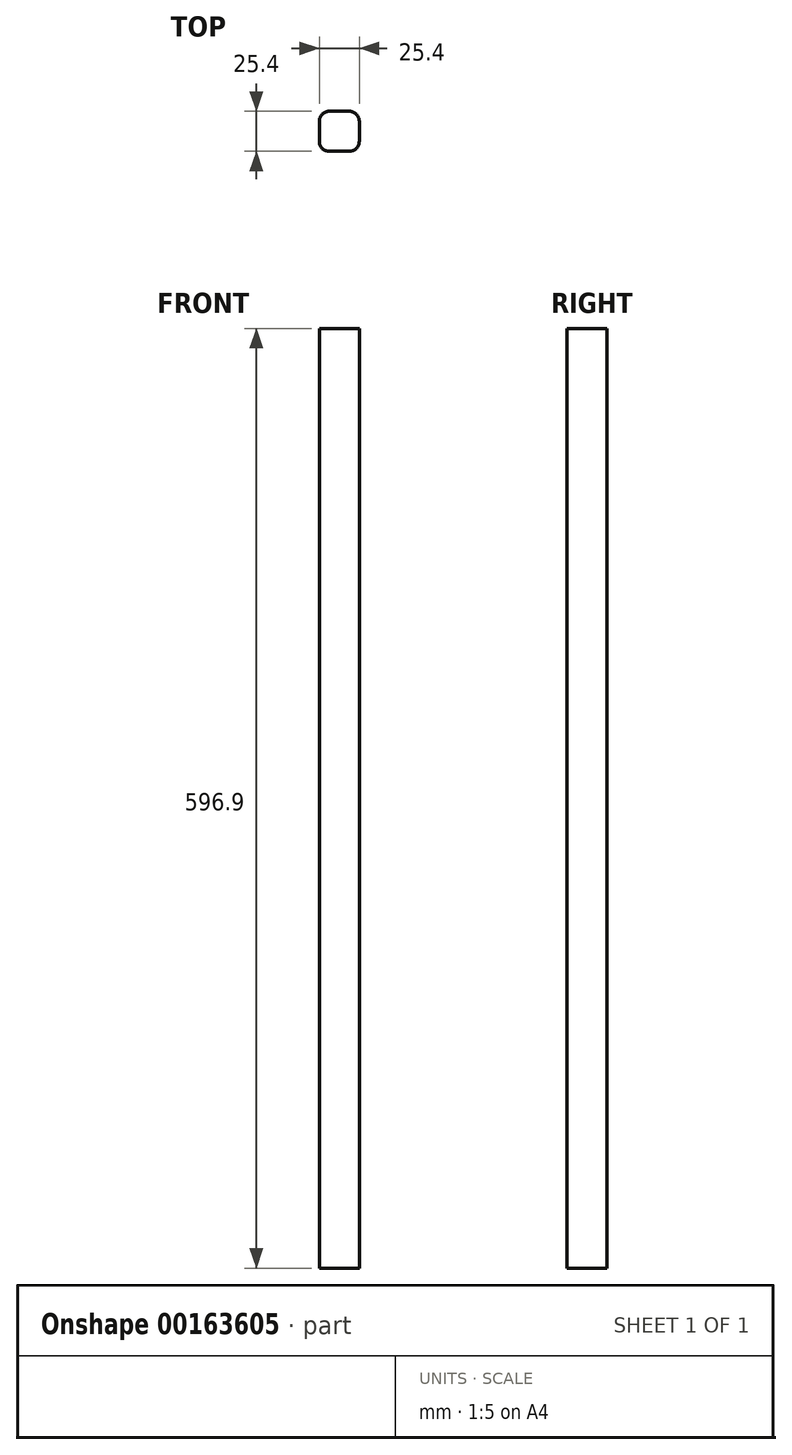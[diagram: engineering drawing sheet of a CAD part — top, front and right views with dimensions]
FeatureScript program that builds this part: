
annotation { "Feature Type Name" : "Feature", "Feature Type Description" : "" }
export const myFeature = defineFeature(function(context is Context, id is Id, definition is map)
    precondition{}
    {
        {
            var Q0;
            Q0=qCreatedBy(makeId("Top.planeOp"),FACE);
            var sketch = newSketch(context, id + "F0", { "sketchPlane" : qUnion([Q0])});
            skLineSegment(sketch, "E0.bottom", {"start": v(6.35, 12.7) * mm, "end": v(-6.35, 12.7) * mm});
            skLineSegment(sketch, "E0.top", {"start": v(6.35, -12.7) * mm, "end": v(-6.35, -12.7) * mm});
            skLineSegment(sketch, "E0.left", {"start": v(12.7, 6.35) * mm, "end": v(12.7, -6.35) * mm});
            skLineSegment(sketch, "E0.right", {"start": v(-12.7, 6.35) * mm, "end": v(-12.7, -6.35) * mm});
            skPoint(sketch, "E0.middle", {"position": v(0, 0) * mm});
            skPoint(sketch, "E1.visualSharp", {"position": v(-12.7, 12.7) * mm});
            skArc(sketch, "E1.filletArc", {"start": v(-6.35, 12.7) * mm, "mid": v(-10.84, 10.84) * mm, "end": v(-12.7, 6.35) * mm});
            skPoint(sketch, "E2.visualSharp", {"position": v(12.7, 12.7) * mm});
            skArc(sketch, "E2.filletArc", {"start": v(12.7, 6.35) * mm, "mid": v(10.84, 10.84) * mm, "end": v(6.35, 12.7) * mm});
            skPoint(sketch, "E3.visualSharp", {"position": v(12.7, -12.7) * mm});
            skArc(sketch, "E3.filletArc", {"start": v(6.35, -12.7) * mm, "mid": v(10.84, -10.84) * mm, "end": v(12.7, -6.35) * mm});
            skPoint(sketch, "E4.visualSharp", {"position": v(-12.7, -12.7) * mm});
            skArc(sketch, "E4.filletArc", {"start": v(-12.7, -6.35) * mm, "mid": v(-10.84, -10.84) * mm, "end": v(-6.35, -12.7) * mm});
            skSolve(sketch);
        }
        {
            var Q0;
            Q0 = qSketchRegion(id + "F0", true);
            extrude(context, id + "F1", {"entities" : qUnion([Q0]), "depth" : 596.9 * mm});
        }
    });
